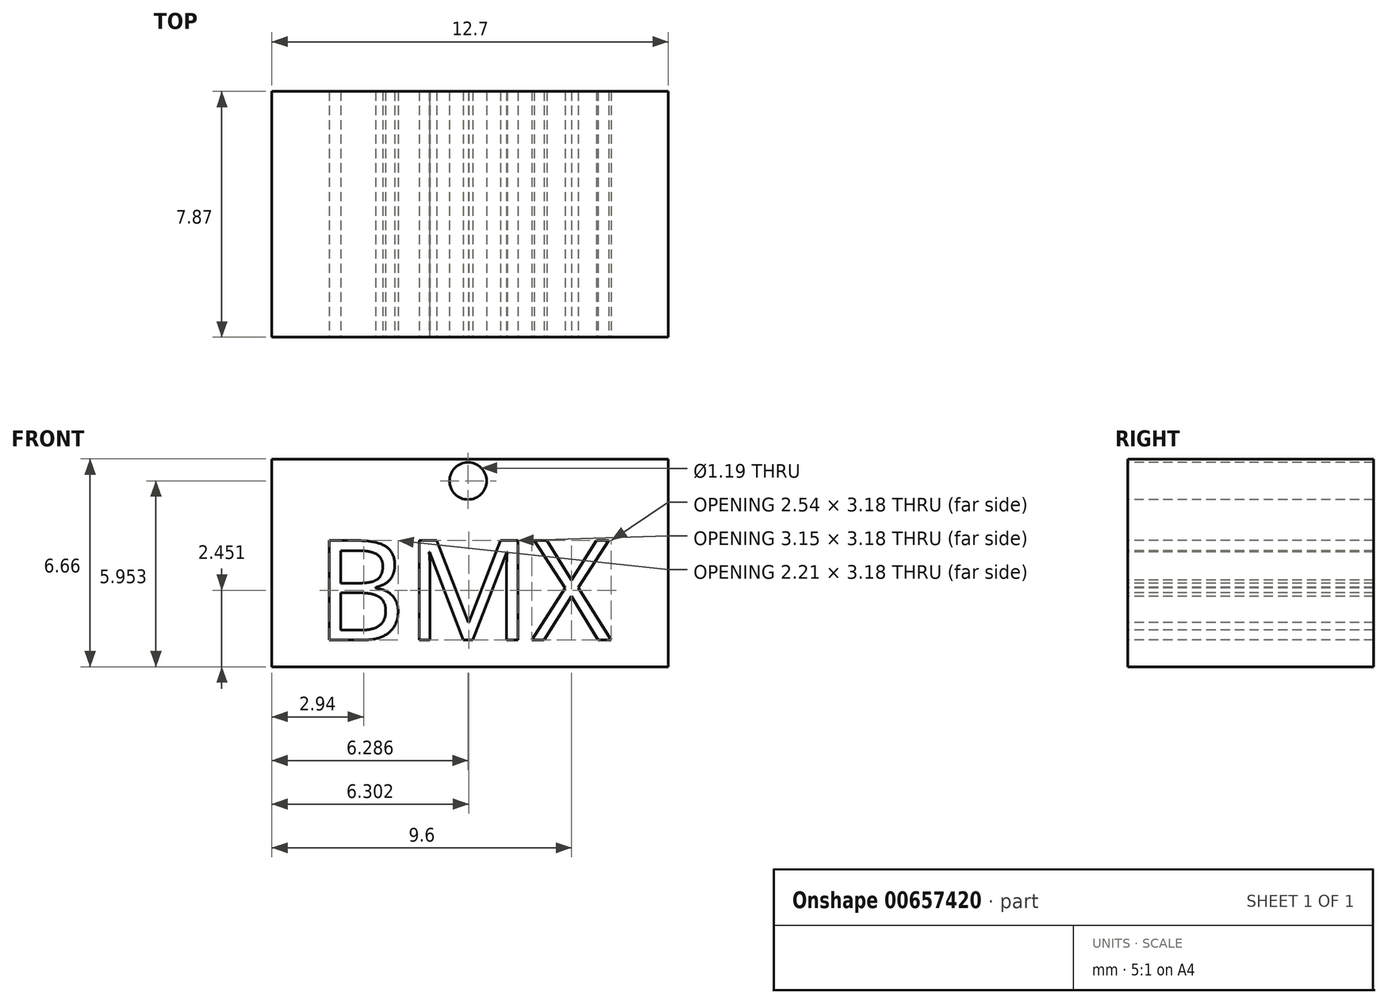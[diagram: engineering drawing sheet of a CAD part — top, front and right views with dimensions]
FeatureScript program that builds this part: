
annotation { "Feature Type Name" : "Feature", "Feature Type Description" : "" }
export const myFeature = defineFeature(function(context is Context, id is Id, definition is map)
    precondition{}
    {
        {
            var Q0;
            Q0=qCreatedBy(makeId("Front.planeOp"),FACE);
            var sketch = newSketch(context, id + "F0", { "sketchPlane" : qUnion([Q0])});
            skLineSegment(sketch, "E0.bottom", {"start": v(-68.35, 64.1) * mm, "end": v(-55.65, 64.1) * mm});
            skLineSegment(sketch, "E0.top", {"start": v(-68.35, 57.44) * mm, "end": v(-55.65, 57.44) * mm});
            skLineSegment(sketch, "E0.left", {"start": v(-68.35, 64.1) * mm, "end": v(-68.35, 57.44) * mm});
            skLineSegment(sketch, "E0.right", {"start": v(-55.65, 64.1) * mm, "end": v(-55.65, 57.44) * mm});
            skSolve(sketch);
        }
        {
            var Q0;
            Q0=makeQuery(id+"F0.imprint","IMPRINT",FACE,{"disambiguationData":[TD([[makeQuery(id+"F0.imprint","IMPRINT",EDGE,{"derivedFrom":sQuery(id+"F0.wireOp",EDGE,"E0.bottom")}),-1.0]])]});
            var sketch = newSketch(context, id + "F1", { "sketchPlane" : qUnion([Q0])});
            skSolve(sketch);
        }
        {
            var Q0;
            Q0=makeQuery(id+"F0.imprint","IMPRINT",FACE,{"disambiguationData":[TD([[makeQuery(id+"F0.imprint","IMPRINT",EDGE,{"derivedFrom":sQuery(id+"F0.wireOp",EDGE,"E0.bottom")}),-1.0]])]});
            var sketch = newSketch(context, id + "F2", { "sketchPlane" : qUnion([Q0])});
            skText(sketch, "E1", { "text": "BMX", "fontName": "OpenSans-Regular.ttf"});
            const initialGuessF2  = {"E1": [-0.06695, 0.0583, 1, 0, 0.00321]};
            skSetInitialGuess(sketch, initialGuessF2);
            skSolve(sketch);
        }
        {
            var Q0;
            Q0=makeQuery(id+"F0.imprint","IMPRINT",FACE,{"disambiguationData":[TD([[makeQuery(id+"F0.imprint","IMPRINT",EDGE,{"derivedFrom":sQuery(id+"F0.wireOp",EDGE,"E0.bottom")}),-1.0]])]});
            extrude(context, id + "F3", {"entities" : qUnion([Q0]), "oppositeDirection" : true, "depth" : 7.87 * mm, "offsetDistance" : 25.4 * mm});
        }
        {
            var Q0;
            Q0 = qSketchRegion(id + "F2", true);
            extrude(context, id + "F4", {"entities" : qUnion([Q0]), "operationType" : NewBodyOperationType.REMOVE, "oppositeDirection" : true, "depth" : 25.4 * mm, "offsetDistance" : 25.4 * mm});
        }
        {
            var Q0;
            Q0=makeQuery(id+"F1.imprint","IMPRINT",FACE,{"disambiguationData":[TD([[makeQuery(id+"F1.imprint","IMPRINT",EDGE,{"derivedFrom":makeQuery(id+"F0.imprint","IMPRINT",EDGE,{"derivedFrom":sQuery(id+"F0.wireOp",EDGE,"E0.bottom")})}),-1.0]])]});
            var sketch = newSketch(context, id + "F5", { "sketchPlane" : qUnion([Q0])});
            skCircle(sketch, "E2", {"center": v(-62.06, 63.4) * mm, "radius": 0.6 * mm});
            skSolve(sketch);
        }
        {
            var Q0;
            Q0=makeQuery(id+"F5.imprint","IMPRINT",FACE,{"disambiguationData":[TD([[makeQuery(id+"F5.imprint","IMPRINT",EDGE,{"derivedFrom":sQuery(id+"F5.wireOp",EDGE,"E2")}),1.0]])]});
            extrude(context, id + "F6", {"entities" : qUnion([Q0]), "operationType" : NewBodyOperationType.REMOVE, "oppositeDirection" : true, "depth" : 25.4 * mm, "offsetDistance" : 25.4 * mm});
        }
    });
